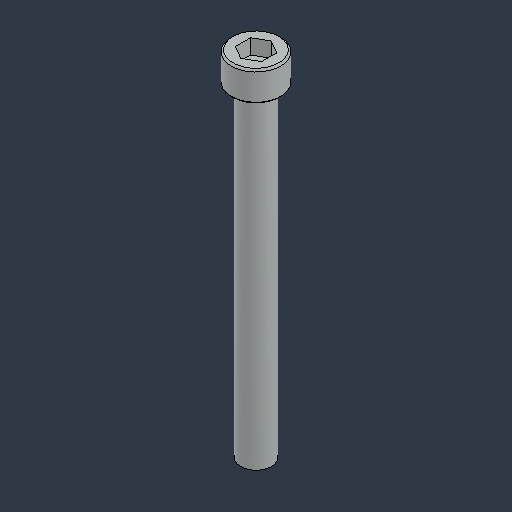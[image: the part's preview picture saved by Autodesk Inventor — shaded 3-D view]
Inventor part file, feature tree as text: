
AUTODESK INVENTOR PART (.ipt)
format: ipt  version: 2024.3 (Build 283343000, 343)  size: 94,720 bytes
history: native  units: in
note: dims shown in document units (in); Inventor stores cm internally (conversion verified against a paired STEP export)
features: chamfer x1
ambient origin geometry x8: Origin, YZ Plane, XZ Plane, XY Plane, X Axis, Y Axis, Z Axis, Center Point
bodies: Solid1 (feature_tree)
feature tree (1):
  chamfer  "Chamfer2"  [1 undecoded]
note: 1 required parameter value undecoded (feature->parameter linkage not recoverable at this tier; creation-order binding heuristic only, values carry confidence <= 0.55)
